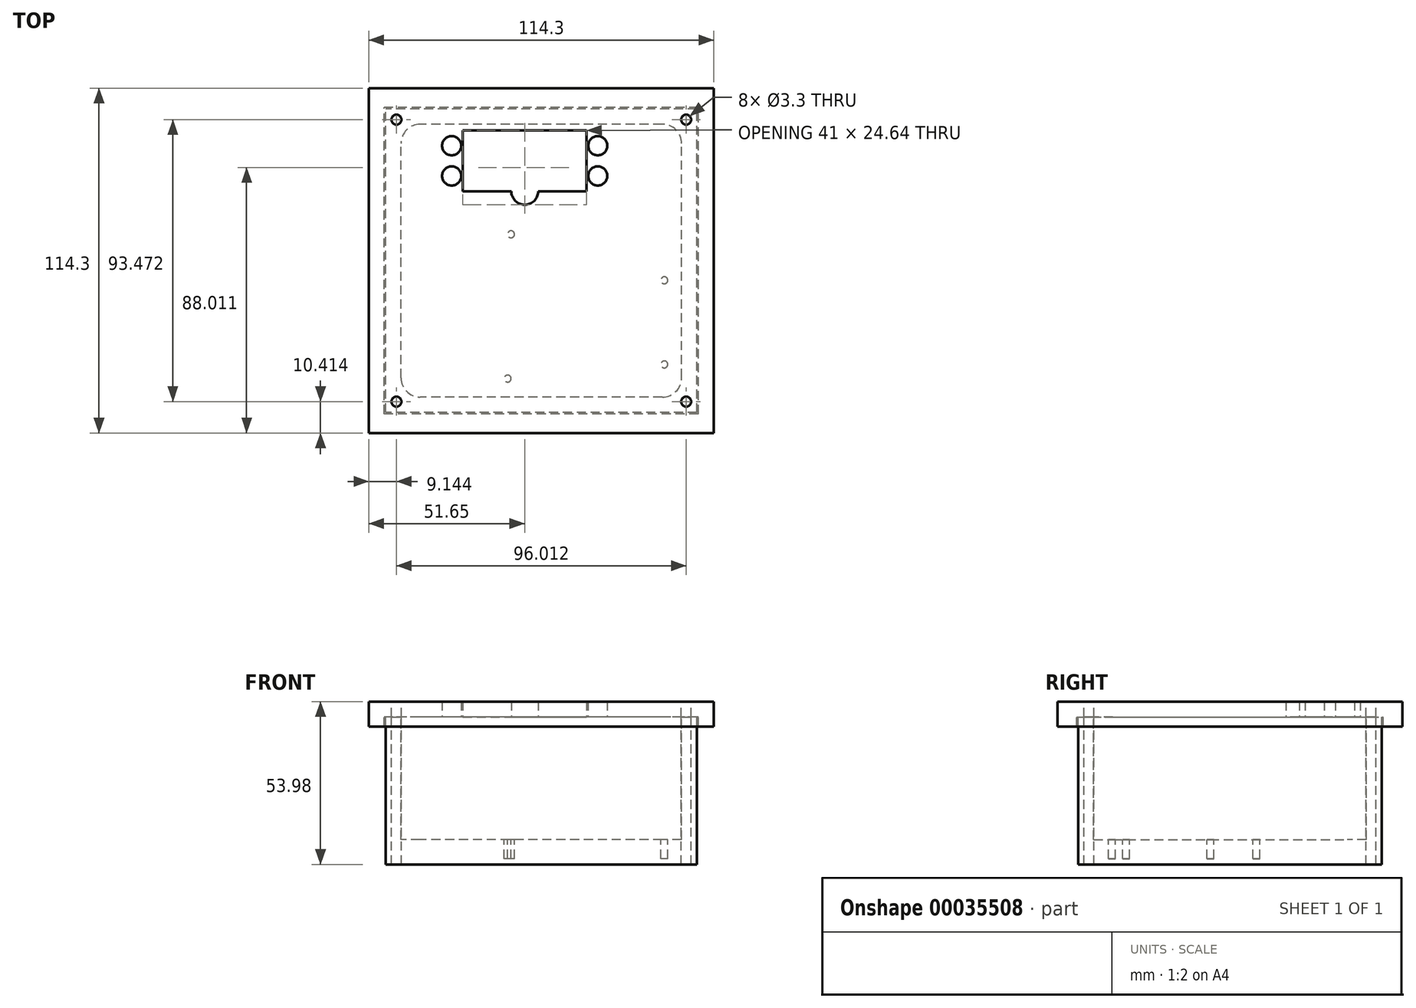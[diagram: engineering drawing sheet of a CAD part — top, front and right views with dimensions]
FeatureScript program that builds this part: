
annotation { "Feature Type Name" : "Feature", "Feature Type Description" : "" }
export const myFeature = defineFeature(function(context is Context, id is Id, definition is map)
    precondition{}
    {
        {
            var Q0;
            Q0=qCreatedBy(makeId("Top.planeOp"),FACE);
            var sketch = newSketch(context, id + "F0", { "sketchPlane" : qUnion([Q0])});
            skLineSegment(sketch, "E0.rect.bottom", {"start": v(57.15, 57.15) * mm, "end": v(-57.15, 57.15) * mm});
            skLineSegment(sketch, "E0.rect.top", {"start": v(57.15, -57.15) * mm, "end": v(-57.15, -57.15) * mm});
            skLineSegment(sketch, "E0.rect.left", {"start": v(57.15, 57.15) * mm, "end": v(57.15, -57.15) * mm});
            skLineSegment(sketch, "E0.rect.right", {"start": v(-57.15, 57.15) * mm, "end": v(-57.15, -57.15) * mm});
            skPoint(sketch, "E0.rect.middle", {"position": v(0, 0) * mm});
            skLineSegment(sketch, "E1.bottom", {"start": v(-26, 43.18) * mm, "end": v(15, 43.18) * mm});
            skLineSegment(sketch, "E1.top", {"start": v(-26, 22.99) * mm, "end": v(15, 22.99) * mm});
            skLineSegment(sketch, "E1.left", {"start": v(-26, 43.18) * mm, "end": v(-26, 22.99) * mm});
            skLineSegment(sketch, "E1.right", {"start": v(15, 43.18) * mm, "end": v(15, 22.99) * mm});
            skLineSegment(sketch, "E2", {"start": v(-5.5, 57.15) * mm, "end": v(-5.5, 43.18) * mm, "construction": true});
            skLineSegment(sketch, "E3.bottom", {"start": v(-29.7, 38.09) * mm, "end": v(18.7, 38.09) * mm, "construction": true});
            skLineSegment(sketch, "E3.top", {"start": v(-29.7, 28.08) * mm, "end": v(18.7, 28.08) * mm, "construction": true});
            skLineSegment(sketch, "E3.left", {"start": v(-29.7, 38.09) * mm, "end": v(-29.7, 28.08) * mm, "construction": true});
            skLineSegment(sketch, "E3.right", {"start": v(18.7, 38.09) * mm, "end": v(18.7, 28.08) * mm, "construction": true});
            skLineSegment(sketch, "E4", {"start": v(15, 33.08) * mm, "end": v(-26, 33.08) * mm, "construction": true});
            skCircle(sketch, "E5", {"center": v(18.7, 38.09) * mm, "radius": 3.18 * mm});
            skCircle(sketch, "E6", {"center": v(18.7, 28.08) * mm, "radius": 3.18 * mm});
            skCircle(sketch, "E7", {"center": v(-29.7, 28.08) * mm, "radius": 3.18 * mm});
            skCircle(sketch, "E8", {"center": v(-29.7, 38.09) * mm, "radius": 3.18 * mm});
            skCircle(sketch, "E9", {"center": v(-5.5, 22.99) * mm, "radius": 4.45 * mm});
            skLineSegment(sketch, "E10", {"start": v(-5.5, 57.15) * mm, "end": v(0, 57.15) * mm});
            skSolve(sketch);
        }
        {
            var Q0;
            Q0 = qSketchRegion(id + "F0", true);
            extrude(context, id + "F1", {"entities" : qUnion([Q0]), "endBound" : BoundingType.SYMMETRIC, "depth" : 5.08 * mm});
        }
        {
            var Q0;
            Q0=makeQuery(id+"F1.opExtrude","CAP_FACE",FACE,{"disambiguationData":[OSD([sQuery(id+"F0.wireOp",EDGE,"E0.rect.bottom"),sQuery(id+"F0.wireOp",EDGE,"E0.rect.top"),sQuery(id+"F0.wireOp",EDGE,"E0.rect.left"),sQuery(id+"F0.wireOp",EDGE,"E0.rect.right"),sQuery(id+"F0.wireOp",EDGE,"E1.bottom"),sQuery(id+"F0.wireOp",EDGE,"E1.top"),sQuery(id+"F0.wireOp",EDGE,"E1.left"),sQuery(id+"F0.wireOp",EDGE,"E1.right"),sQuery(id+"F0.wireOp",EDGE,"E5"),sQuery(id+"F0.wireOp",EDGE,"E6"),sQuery(id+"F0.wireOp",EDGE,"E7"),sQuery(id+"F0.wireOp",EDGE,"E8")])],"isStart":true});
            var sketch = newSketch(context, id + "F2", { "sketchPlane" : qUnion([Q0])});
            skLineSegment(sketch, "E11.rect.bottom", {"start": v(57.15, 57.15) * mm, "end": v(-57.15, 57.15) * mm});
            skLineSegment(sketch, "E11.rect.top", {"start": v(57.15, -57.15) * mm, "end": v(-57.15, -57.15) * mm});
            skLineSegment(sketch, "E11.rect.left", {"start": v(57.15, 57.15) * mm, "end": v(57.15, -57.15) * mm});
            skLineSegment(sketch, "E11.rect.right", {"start": v(-57.15, 57.15) * mm, "end": v(-57.15, -57.15) * mm});
            skPoint(sketch, "E11.rect.middle", {"position": v(0, 0) * mm});
            skLineSegment(sketch, "E12.rect.bottom", {"start": v(52.07, 50.8) * mm, "end": v(-52.07, 50.8) * mm});
            skLineSegment(sketch, "E12.rect.top", {"start": v(52.07, -50.8) * mm, "end": v(-52.07, -50.8) * mm});
            skLineSegment(sketch, "E12.rect.left", {"start": v(52.07, 50.8) * mm, "end": v(52.07, -50.8) * mm});
            skLineSegment(sketch, "E12.rect.right", {"start": v(-52.07, 50.8) * mm, "end": v(-52.07, -50.8) * mm});
            skSolve(sketch);
        }
        {
            var Q0;
            Q0 = qSketchRegion(id + "F2", true);
            extrude(context, id + "F3", {"entities" : qUnion([Q0]), "operationType" : NewBodyOperationType.ADD, "depth" : 3.17 * mm});
        }
        {
            var Q0;
            Q0=makeQuery(id+"F1.opExtrude","CAP_FACE",FACE,{"disambiguationData":[OSD([sQuery(id+"F0.wireOp",EDGE,"E0.rect.bottom"),sQuery(id+"F0.wireOp",EDGE,"E0.rect.top"),sQuery(id+"F0.wireOp",EDGE,"E0.rect.left"),sQuery(id+"F0.wireOp",EDGE,"E0.rect.right"),sQuery(id+"F0.wireOp",EDGE,"E1.bottom"),sQuery(id+"F0.wireOp",EDGE,"E1.top"),sQuery(id+"F0.wireOp",EDGE,"E1.left"),sQuery(id+"F0.wireOp",EDGE,"E1.right"),sQuery(id+"F0.wireOp",EDGE,"E5"),sQuery(id+"F0.wireOp",EDGE,"E6"),sQuery(id+"F0.wireOp",EDGE,"E7"),sQuery(id+"F0.wireOp",EDGE,"E8")])],"isStart":true});
            var sketch = newSketch(context, id + "F4", { "sketchPlane" : qUnion([Q0])});
            skLineSegment(sketch, "E13.rect.bottom", {"start": v(51.56, 50.3) * mm, "end": v(-51.56, 50.3) * mm});
            skLineSegment(sketch, "E13.rect.top", {"start": v(51.56, -50.3) * mm, "end": v(-51.56, -50.3) * mm});
            skLineSegment(sketch, "E13.rect.left", {"start": v(51.56, 50.3) * mm, "end": v(51.56, -50.3) * mm});
            skLineSegment(sketch, "E13.rect.right", {"start": v(-51.56, 50.3) * mm, "end": v(-51.56, -50.3) * mm});
            skPoint(sketch, "E13.rect.middle", {"position": v(0, 0) * mm});
            skLineSegment(sketch, "E14.rect.bottom", {"start": v(46.48, 45.21) * mm, "end": v(-46.48, 45.21) * mm});
            skLineSegment(sketch, "E14.rect.top", {"start": v(46.48, -45.21) * mm, "end": v(-46.48, -45.21) * mm});
            skLineSegment(sketch, "E14.rect.left", {"start": v(46.48, 45.21) * mm, "end": v(46.48, -45.21) * mm});
            skLineSegment(sketch, "E14.rect.right", {"start": v(-46.48, 45.21) * mm, "end": v(-46.48, -45.21) * mm});
            skSolve(sketch);
        }
        {
            var Q0;
            Q0 = qSketchRegion(id + "F4", true);
            extrude(context, id + "F5", {"entities" : qUnion([Q0]), "depth" : 48.9 * mm});
        }
        {
            var Q0;
            Q0=makeQuery(id+"F5.opExtrude","CAP_FACE",FACE,{"disambiguationData":[OSD([sQuery(id+"F4.wireOp",EDGE,"E13.rect.bottom"),sQuery(id+"F4.wireOp",EDGE,"E13.rect.top"),sQuery(id+"F4.wireOp",EDGE,"E13.rect.left"),sQuery(id+"F4.wireOp",EDGE,"E13.rect.right"),sQuery(id+"F4.wireOp",EDGE,"E14.rect.bottom"),sQuery(id+"F4.wireOp",EDGE,"E14.rect.top"),sQuery(id+"F4.wireOp",EDGE,"E14.rect.left"),sQuery(id+"F4.wireOp",EDGE,"E14.rect.right")])],"isStart":false});
            var sketch = newSketch(context, id + "F6", { "sketchPlane" : qUnion([Q0])});
            skLineSegment(sketch, "E15.bottom", {"start": v(-51.56, 50.3) * mm, "end": v(51.56, 50.3) * mm});
            skLineSegment(sketch, "E15.top", {"start": v(-51.56, -50.3) * mm, "end": v(51.56, -50.3) * mm});
            skLineSegment(sketch, "E15.left", {"start": v(-51.56, 50.3) * mm, "end": v(-51.56, -50.3) * mm});
            skLineSegment(sketch, "E15.right", {"start": v(51.56, 50.3) * mm, "end": v(51.56, -50.3) * mm});
            skSolve(sketch);
        }
        {
            var Q0;
            Q0 = qSketchRegion(id + "F6", true);
            extrude(context, id + "F7", {"entities" : qUnion([Q0]), "operationType" : NewBodyOperationType.ADD, "oppositeDirection" : true, "depth" : 8.25 * mm});
        }
        {
            var Q0;
            Q0=makeQuery(id+"F7.opExtrude","CAP_FACE",FACE,{"disambiguationData":[OSD([sQuery(id+"F6.wireOp",EDGE,"E15.bottom"),sQuery(id+"F6.wireOp",EDGE,"E15.top"),sQuery(id+"F6.wireOp",EDGE,"E15.left"),sQuery(id+"F6.wireOp",EDGE,"E15.right")])],"isStart":false});
            var sketch = newSketch(context, id + "F8", { "sketchPlane" : qUnion([Q0])});
            skPoint(sketch, "E16", {"position": v(-10.03, 8.72) * mm});
            skPoint(sketch, "E17", {"position": v(-11.13, -39.12) * mm});
            skPoint(sketch, "E18", {"position": v(40.77, -6.52) * mm});
            skPoint(sketch, "E19", {"position": v(40.77, -34.42) * mm});
            skLineSegment(sketch, "E20.bottom", {"start": v(-25.27, 11.3) * mm, "end": v(43.3, 11.3) * mm, "construction": true});
            skLineSegment(sketch, "E20.top", {"start": v(-25.27, -42.04) * mm, "end": v(43.3, -42.04) * mm, "construction": true});
            skLineSegment(sketch, "E20.left", {"start": v(-25.27, 11.3) * mm, "end": v(-25.27, -42.04) * mm, "construction": true});
            skLineSegment(sketch, "E20.right", {"start": v(43.3, 11.3) * mm, "end": v(43.3, -42.04) * mm, "construction": true});
            skCircle(sketch, "E21", {"center": v(-10.03, 8.72) * mm, "radius": 1.14 * mm});
            skCircle(sketch, "E22", {"center": v(40.77, -6.52) * mm, "radius": 1.14 * mm});
            skCircle(sketch, "E23", {"center": v(40.77, -34.42) * mm, "radius": 1.14 * mm});
            skCircle(sketch, "E24", {"center": v(-11.13, -39.12) * mm, "radius": 1.14 * mm});
            skSolve(sketch);
        }
        {
            var Q0;
            Q0 = qSketchRegion(id + "F8", true);
            extrude(context, id + "F9", {"entities" : qUnion([Q0]), "operationType" : NewBodyOperationType.REMOVE, "oppositeDirection" : true, "depth" : 6.35 * mm});
        }
        {
            var Q0;
            Q0=makeQuery(id+"F5.opExtrude","SWEPT_EDGE",EDGE,{"disambiguationData":[OSD([sQuery(id+"F4.wireOp",EDGE,"E14.rect.top"),sQuery(id+"F4.wireOp",EDGE,"E14.rect.right")])]});
            var Q1;
            Q1=makeQuery(id+"F5.opExtrude","SWEPT_EDGE",EDGE,{"disambiguationData":[OSD([sQuery(id+"F4.wireOp",EDGE,"E14.rect.top"),sQuery(id+"F4.wireOp",EDGE,"E14.rect.left")])]});
            var Q2;
            Q2=makeQuery(id+"F5.opExtrude","SWEPT_EDGE",EDGE,{"disambiguationData":[OSD([sQuery(id+"F4.wireOp",EDGE,"E14.rect.bottom"),sQuery(id+"F4.wireOp",EDGE,"E14.rect.left")])]});
            var Q3;
            Q3=makeQuery(id+"F5.opExtrude","SWEPT_EDGE",EDGE,{"disambiguationData":[OSD([sQuery(id+"F4.wireOp",EDGE,"E14.rect.bottom"),sQuery(id+"F4.wireOp",EDGE,"E14.rect.right")])]});
            fillet(context, id + "F10", {"entities" : qUnion([Q0, Q1, Q2, Q3]), "radius" : 6.35 * mm, "tangentPropagation" : true, "allowEdgeOverflow" : false});
        }
        {
            var Q0;
            Q0=makeQuery(id+"F5.opExtrude","CAP_FACE",FACE,{"disambiguationData":[OSD([sQuery(id+"F4.wireOp",EDGE,"E13.rect.bottom"),sQuery(id+"F4.wireOp",EDGE,"E13.rect.top"),sQuery(id+"F4.wireOp",EDGE,"E13.rect.left"),sQuery(id+"F4.wireOp",EDGE,"E13.rect.right"),sQuery(id+"F4.wireOp",EDGE,"E14.rect.bottom"),sQuery(id+"F4.wireOp",EDGE,"E14.rect.top"),sQuery(id+"F4.wireOp",EDGE,"E14.rect.left"),sQuery(id+"F4.wireOp",EDGE,"E14.rect.right")])],"isStart":true});
            var sketch = newSketch(context, id + "F11", { "sketchPlane" : qUnion([Q0])});
            skLineSegment(sketch, "E25.rect.bottom", {"start": v(48, 46.74) * mm, "end": v(-48, 46.74) * mm, "construction": true});
            skLineSegment(sketch, "E25.rect.top", {"start": v(48, -46.74) * mm, "end": v(-48, -46.74) * mm, "construction": true});
            skLineSegment(sketch, "E25.rect.left", {"start": v(48, 46.74) * mm, "end": v(48, -46.74) * mm, "construction": true});
            skLineSegment(sketch, "E25.rect.right", {"start": v(-48, 46.74) * mm, "end": v(-48, -46.74) * mm, "construction": true});
            skPoint(sketch, "E25.rect.middle", {"position": v(0, 0) * mm});
            skCircle(sketch, "E26", {"center": v(-48, 46.74) * mm, "radius": 1.14 * mm});
            skCircle(sketch, "E27", {"center": v(48, 46.74) * mm, "radius": 1.14 * mm});
            skCircle(sketch, "E28", {"center": v(48, -46.74) * mm, "radius": 1.14 * mm});
            skCircle(sketch, "E29", {"center": v(-48, -46.74) * mm, "radius": 1.14 * mm});
            skSolve(sketch);
        }
        {
            var Q0;
            Q0 = qSketchRegion(id + "F11", true);
            extrude(context, id + "F12", {"entities" : qUnion([Q0]), "operationType" : NewBodyOperationType.REMOVE, "oppositeDirection" : true, "depth" : 12.7 * mm});
        }
        {
            var Q0;
            Q0=makeQuery(id+"F1.opExtrude","CAP_FACE",FACE,{"disambiguationData":[OSD([sQuery(id+"F0.wireOp",EDGE,"E0.rect.bottom"),sQuery(id+"F0.wireOp",EDGE,"E0.rect.top"),sQuery(id+"F0.wireOp",EDGE,"E0.rect.left"),sQuery(id+"F0.wireOp",EDGE,"E0.rect.right"),sQuery(id+"F0.wireOp",EDGE,"E1.bottom"),sQuery(id+"F0.wireOp",EDGE,"E1.top"),sQuery(id+"F0.wireOp",EDGE,"E1.left"),sQuery(id+"F0.wireOp",EDGE,"E1.right"),sQuery(id+"F0.wireOp",EDGE,"E5"),sQuery(id+"F0.wireOp",EDGE,"E6"),sQuery(id+"F0.wireOp",EDGE,"E7"),sQuery(id+"F0.wireOp",EDGE,"E8"),sQuery(id+"F0.wireOp",EDGE,"E9")])],"isStart":false});
            var sketch = newSketch(context, id + "F13", { "sketchPlane" : qUnion([Q0])});
            skPoint(sketch, "E30.0", {"position": v(-48, -46.74) * mm});
            skPoint(sketch, "E30.1", {"position": v(48, -46.74) * mm});
            skPoint(sketch, "E30.2", {"position": v(48, 46.74) * mm});
            skPoint(sketch, "E30.3", {"position": v(-48, 46.74) * mm});
            skCircle(sketch, "E31", {"center": v(-48, -46.74) * mm, "radius": 1.65 * mm});
            skCircle(sketch, "E32", {"center": v(-48, 46.74) * mm, "radius": 1.65 * mm});
            skCircle(sketch, "E33", {"center": v(48, 46.74) * mm, "radius": 1.65 * mm});
            skCircle(sketch, "E34", {"center": v(48, -46.74) * mm, "radius": 1.65 * mm});
            skSolve(sketch);
        }
        {
            var Q0;
            Q0 = qSketchRegion(id + "F13", true);
            extrude(context, id + "F14", {"entities" : qUnion([Q0]), "operationType" : NewBodyOperationType.REMOVE, "endBound" : BoundingType.THROUGH_ALL, "oppositeDirection" : true, "depth" : 25.4 * mm});
        }
    });
